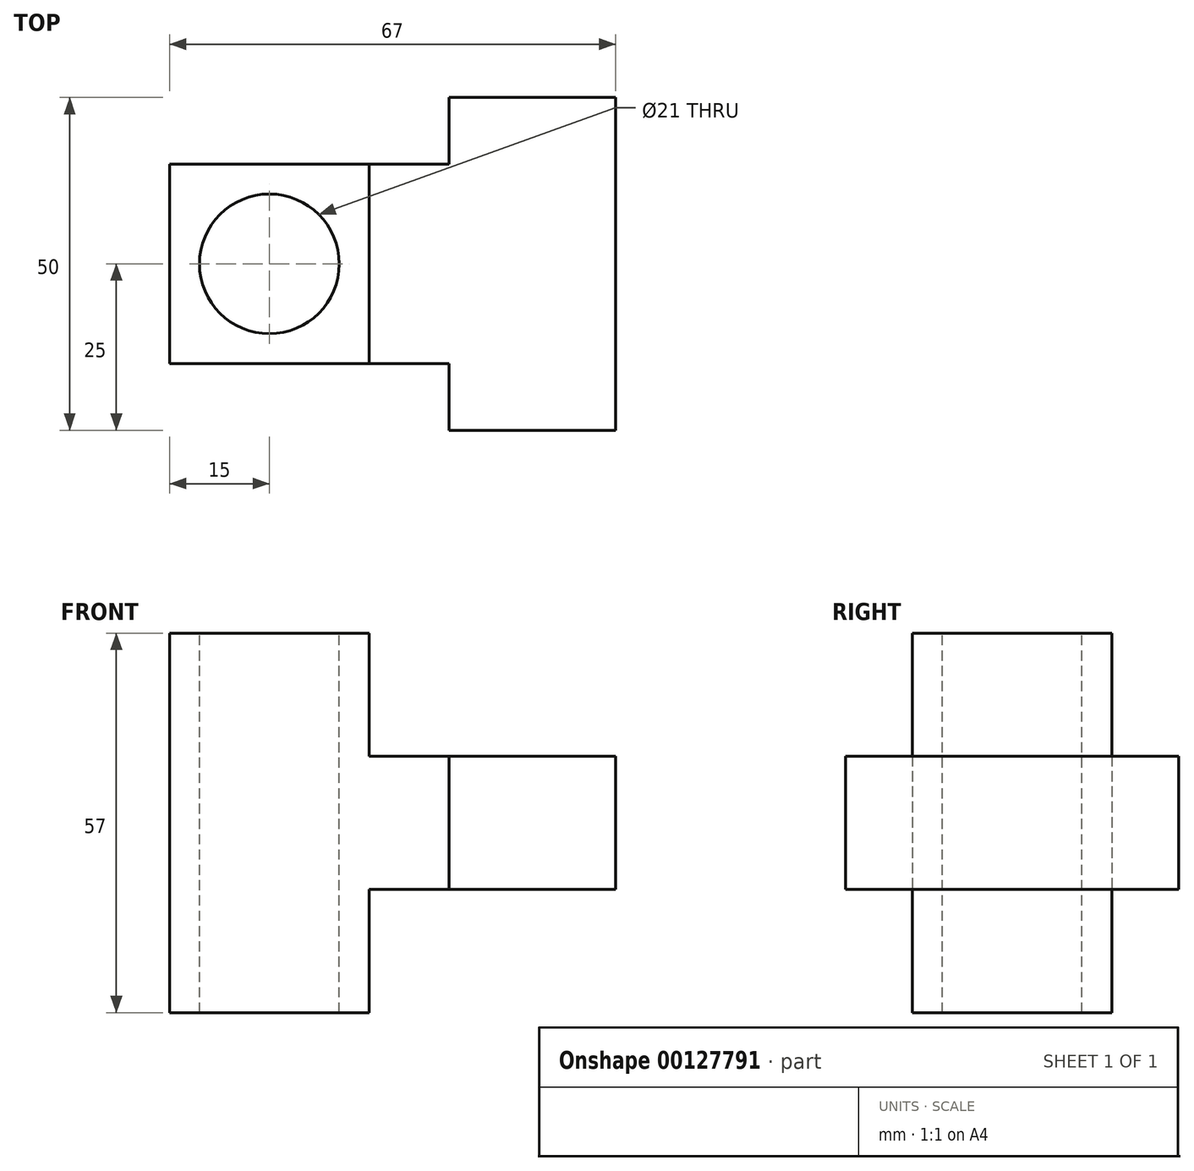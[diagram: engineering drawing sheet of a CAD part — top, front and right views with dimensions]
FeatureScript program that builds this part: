
annotation { "Feature Type Name" : "Feature", "Feature Type Description" : "" }
export const myFeature = defineFeature(function(context is Context, id is Id, definition is map)
    precondition{}
    {
        {
            var Q0;
            Q0=qCreatedBy(makeId("Top.planeOp"),FACE);
            var sketch = newSketch(context, id + "F0", { "sketchPlane" : qUnion([Q0])});
            skLineSegment(sketch, "E0.bottom", {"start": v(12.5, -25) * mm, "end": v(-12.5, -25) * mm});
            skLineSegment(sketch, "E0.top", {"start": v(12.5, 25) * mm, "end": v(-12.5, 25) * mm});
            skLineSegment(sketch, "E0.left", {"start": v(12.5, -25) * mm, "end": v(12.5, 25) * mm});
            skLineSegment(sketch, "E0.right", {"start": v(-12.5, -25) * mm, "end": v(-12.5, -15) * mm});
            skPoint(sketch, "E0.middle", {"position": v(0, 0) * mm});
            skLineSegment(sketch, "E1", {"start": v(-12.5, 15) * mm, "end": v(-54.5, 15) * mm});
            skLineSegment(sketch, "E2", {"start": v(-54.5, 15) * mm, "end": v(-54.5, -15) * mm});
            skLineSegment(sketch, "E3", {"start": v(-54.5, -15) * mm, "end": v(-12.5, -15) * mm});
            skLineSegment(sketch, "E4.trimOffspring", {"start": v(-12.5, 15) * mm, "end": v(-12.5, 25) * mm});
            skLineSegment(sketch, "E5", {"start": v(0, 0) * mm, "end": v(-23.93, 0) * mm, "construction": true});
            skSolve(sketch);
        }
        {
            var Q0;
            Q0 = qSketchRegion(id + "F0", true);
            extrude(context, id + "F1", {"entities" : qUnion([Q0]), "endBound" : BoundingType.SYMMETRIC, "depth" : 20 * mm});
        }
        {
            var Q0;
            Q0=qCreatedBy(makeId("Top.planeOp"),FACE);
            var sketch = newSketch(context, id + "F2", { "sketchPlane" : qUnion([Q0])});
            skLineSegment(sketch, "E6.bottom", {"start": v(-54.5, 15) * mm, "end": v(-24.5, 15) * mm});
            skLineSegment(sketch, "E6.top", {"start": v(-54.5, -15) * mm, "end": v(-24.5, -15) * mm});
            skLineSegment(sketch, "E6.left", {"start": v(-54.5, 15) * mm, "end": v(-54.5, -15) * mm});
            skLineSegment(sketch, "E6.right", {"start": v(-24.5, 15) * mm, "end": v(-24.5, -15) * mm});
            skSolve(sketch);
        }
        {
            var Q0;
            Q0 = qSketchRegion(id + "F2", true);
            extrude(context, id + "F3", {"entities" : qUnion([Q0]), "operationType" : NewBodyOperationType.ADD, "endBound" : BoundingType.SYMMETRIC, "depth" : 57 * mm});
        }
        {
            var Q0;
            Q0=makeQuery(id+"F3.opExtrude","CAP_FACE",FACE,{"disambiguationData":[OSD([sQuery(id+"F2.wireOp",EDGE,"E6.bottom"),sQuery(id+"F2.wireOp",EDGE,"E6.top"),sQuery(id+"F2.wireOp",EDGE,"E6.left"),sQuery(id+"F2.wireOp",EDGE,"E6.right")])],"isStart":false});
            var sketch = newSketch(context, id + "F4", { "sketchPlane" : qUnion([Q0])});
            skCircle(sketch, "E7", {"center": v(-39.5, 0) * mm, "radius": 10.5 * mm});
            skSolve(sketch);
        }
        {
            var Q0;
            Q0 = qSketchRegion(id + "F4", true);
            extrude(context, id + "F5", {"entities" : qUnion([Q0]), "operationType" : NewBodyOperationType.REMOVE, "endBound" : BoundingType.THROUGH_ALL, "oppositeDirection" : true, "depth" : 25 * mm});
        }
    });
